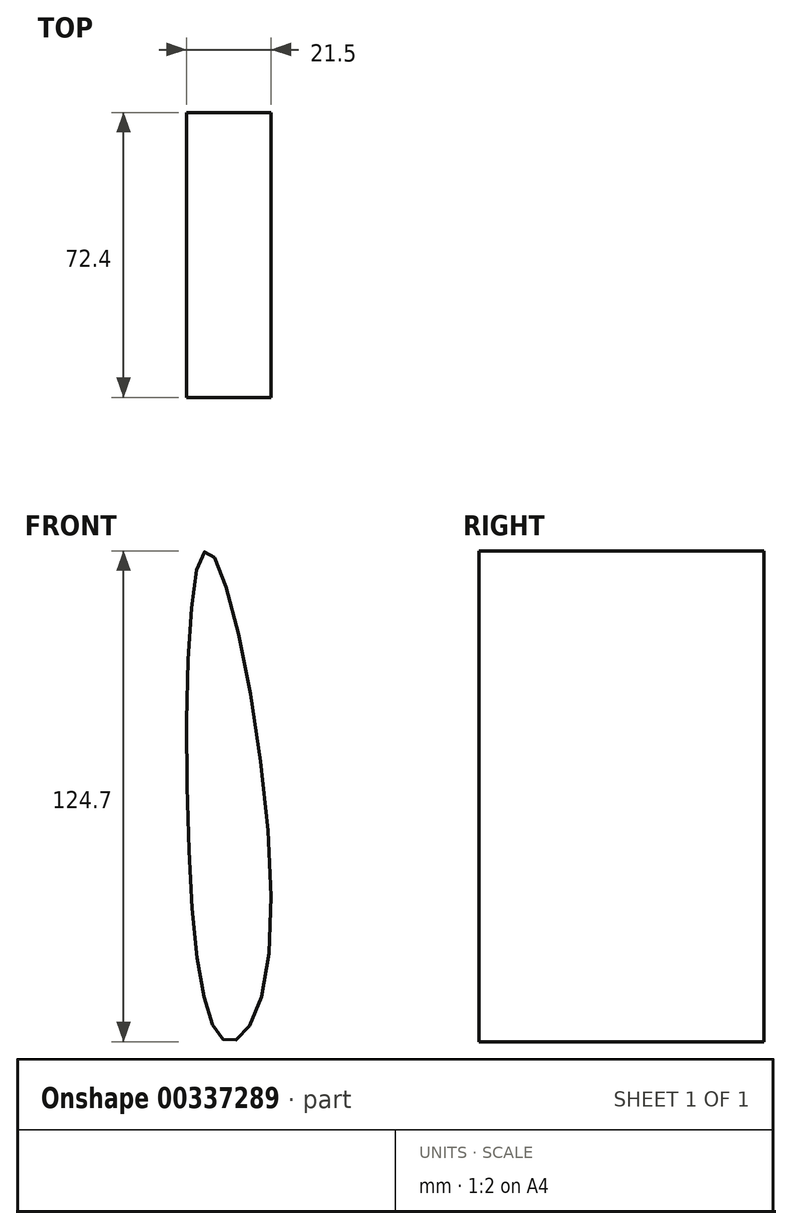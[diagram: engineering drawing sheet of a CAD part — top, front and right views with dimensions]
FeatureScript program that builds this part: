
annotation { "Feature Type Name" : "Feature", "Feature Type Description" : "" }
export const myFeature = defineFeature(function(context is Context, id is Id, definition is map)
    precondition{}
    {
        {
            var Q0;
            Q0=qCreatedBy(makeId("Front.planeOp"),FACE);
            var sketch = newSketch(context, id + "F0", { "sketchPlane" : qUnion([Q0])});
            skFitSpline(sketch, "E0", {"points": [v(36.75, 22.36) * mm, v(21.33, 124.52) * mm, v(16.54, 44.78) * mm, v(26, 0) * mm, v(36.75, 22.36) * mm]});
            skSolve(sketch);
        }
        {
            var Q0;
            Q0=sQuery(id+"F0.wireOp",EDGE,"E0");
            extrude(context, id + "F1", {"bodyType" : ToolBodyType.SURFACE, "surfaceEntities" : qUnion([Q0]), "depth" : 72.4 * mm});
        }
    });
